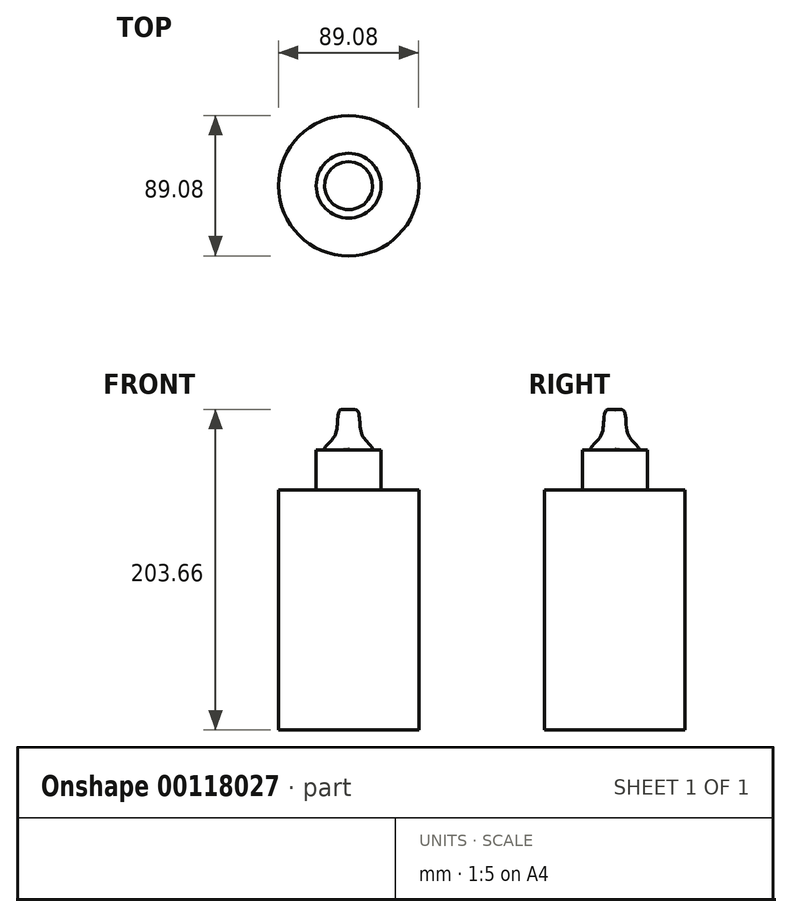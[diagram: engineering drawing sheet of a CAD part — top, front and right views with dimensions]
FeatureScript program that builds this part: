
annotation { "Feature Type Name" : "Feature", "Feature Type Description" : "" }
export const myFeature = defineFeature(function(context is Context, id is Id, definition is map)
    precondition{}
    {
        {
            var Q0;
            Q0=qCreatedBy(makeId("Top.planeOp"),FACE);
            var sketch = newSketch(context, id + "F0", { "sketchPlane" : qUnion([Q0])});
            skCircle(sketch, "E0", {"center": v(0, 0) * mm, "radius": 44.54 * mm});
            skSolve(sketch);
        }
        {
            var Q0;
            Q0=makeQuery(id+"F0.imprint","IMPRINT",FACE,{"disambiguationData":[TD([[makeQuery(id+"F0.imprint","IMPRINT",EDGE,{"derivedFrom":sQuery(id+"F0.wireOp",EDGE,"E0")}),1.0]])]});
            extrude(context, id + "F1", {"entities" : qUnion([Q0]), "depth" : 152.4 * mm});
        }
        {
            var Q0;
            Q0=makeQuery(id+"F1.opExtrude","CAP_FACE",FACE,{"disambiguationData":[OSD([sQuery(id+"F0.wireOp",EDGE,"E0")])],"isStart":false});
            var sketch = newSketch(context, id + "F2", { "sketchPlane" : qUnion([Q0])});
            skCircle(sketch, "E1", {"center": v(0, 0) * mm, "radius": 20.6 * mm});
            skSolve(sketch);
        }
        {
            var Q0;
            Q0=makeQuery(id+"F2.imprint","IMPRINT",FACE,{"disambiguationData":[TD([[makeQuery(id+"F2.imprint","IMPRINT",EDGE,{"derivedFrom":sQuery(id+"F2.wireOp",EDGE,"E1")}),1.0]])]});
            extrude(context, id + "F3", {"entities" : qUnion([Q0]), "operationType" : NewBodyOperationType.ADD, "depth" : 25.4 * mm});
        }
        {
            var Q0;
            Q0=qCreatedBy(makeId("Right.planeOp"),FACE);
            var sketch = newSketch(context, id + "F4", { "sketchPlane" : qUnion([Q0])});
            skLineSegment(sketch, "E2", {"start": v(0, 178.73) * mm, "end": v(0, 202.9) * mm});
            skFitSpline(sketch, "E3", {"points": [v(0, 202.9) * mm, v(5.63, 202.9) * mm, v(7.7, 189.98) * mm, v(12.7, 182.07) * mm, v(15.21, 178.32) * mm, v(0, 178.73) * mm], "startDerivative": vector(42.5, 12.48) * mm, "endDerivative": vector(-83.6, 10.78) * mm});
            skSolve(sketch);
        }
        {
            var Q0;
            Q0=makeQuery(id+"F4.imprint","IMPRINT",FACE,{"disambiguationData":[TD([[makeQuery(id+"F4.imprint","IMPRINT",EDGE,{"derivedFrom":sQuery(id+"F4.wireOp",EDGE,"E2")}),-1.0]])]});
            var Q1;
            Q1=sQuery(id+"F4.wireOp",EDGE,"E2");
            revolve(context, id + "F5", {"entities" : qUnion([Q0]), "axis" : qUnion([Q1]), "revolveType" : RevolveType.FULL});
        }
    });
